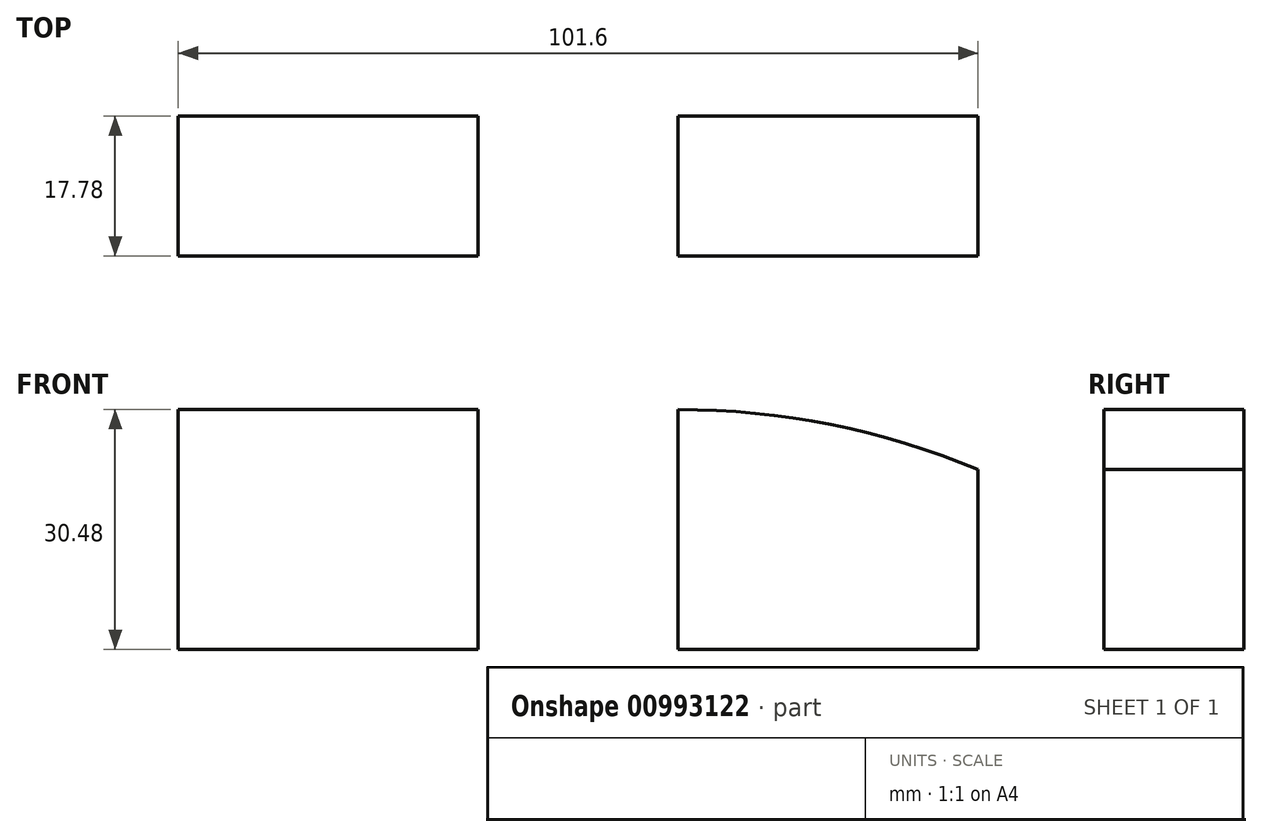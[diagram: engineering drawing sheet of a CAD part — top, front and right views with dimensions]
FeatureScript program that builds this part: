
annotation { "Feature Type Name" : "Feature", "Feature Type Description" : "" }
export const myFeature = defineFeature(function(context is Context, id is Id, definition is map)
    precondition{}
    {
        {
            var Q0;
            Q0=qCreatedBy(makeId("Top.planeOp"),FACE);
            var sketch = newSketch(context, id + "F0", { "sketchPlane" : qUnion([Q0])});
            skLineSegment(sketch, "E0.bottom", {"start": v(-38.1, -30.06) * mm, "end": v(63.5, -30.06) * mm});
            skLineSegment(sketch, "E0.top", {"start": v(-38.1, -47.84) * mm, "end": v(63.5, -47.84) * mm});
            skLineSegment(sketch, "E0.left", {"start": v(-38.1, -30.06) * mm, "end": v(-38.1, -47.84) * mm});
            skLineSegment(sketch, "E0.right", {"start": v(63.5, -30.06) * mm, "end": v(63.5, -47.84) * mm});
            skLineSegment(sketch, "E1.bottom", {"start": v(0, -30.06) * mm, "end": v(25.4, -30.06) * mm});
            skLineSegment(sketch, "E1.top", {"start": v(0, -47.84) * mm, "end": v(25.4, -47.84) * mm});
            skLineSegment(sketch, "E1.left", {"start": v(0, -30.06) * mm, "end": v(0, -47.84) * mm});
            skLineSegment(sketch, "E1.right", {"start": v(25.4, -30.06) * mm, "end": v(25.4, -47.84) * mm});
            skSolve(sketch);
        }
        {
            var Q0;
            {var subQ0=sQuery(id+"F0.wireOp",EDGE,"E0.left");Q0=makeQuery(id+"F0.imprint","IMPRINT",FACE,{"disambiguationData":[TD([[makeQuery(id+"F0.imprint","IMPRINT",EDGE,{"derivedFrom":subQ0}),1.0]])]});}
            var Q1;
            Q1=makeQuery(id+"F0.imprint","IMPRINT",FACE,{"disambiguationData":[TD([[makeQuery(id+"F0.imprint","IMPRINT",EDGE,{"derivedFrom":sQuery(id+"F0.wireOp",EDGE,"E1.bottom")}),-1.0]])]});
            var Q2;
            {var subQ0=sQuery(id+"F0.wireOp",EDGE,"E0.right");Q2=makeQuery(id+"F0.imprint","IMPRINT",FACE,{"disambiguationData":[TD([[makeQuery(id+"F0.imprint","IMPRINT",EDGE,{"derivedFrom":subQ0}),-1.0]])]});}
            extrude(context, id + "F1", {"entities" : qUnion([Q0, Q1, Q2]), "oppositeDirection" : true, "depth" : 15.24 * mm, "offsetDistance" : 25.4 * mm});
        }
        {
            var Q0;
            {var subQ0=sQuery(id+"F0.wireOp",EDGE,"E0.left");Q0=makeQuery(id+"F0.imprint","IMPRINT",FACE,{"disambiguationData":[TD([[makeQuery(id+"F0.imprint","IMPRINT",EDGE,{"derivedFrom":subQ0}),1.0]])]});}
            var Q1;
            {var subQ0=sQuery(id+"F0.wireOp",EDGE,"E0.right");Q1=makeQuery(id+"F0.imprint","IMPRINT",FACE,{"disambiguationData":[TD([[makeQuery(id+"F0.imprint","IMPRINT",EDGE,{"derivedFrom":subQ0}),-1.0]])]});}
            extrude(context, id + "F2", {"entities" : qUnion([Q0, Q1]), "operationType" : NewBodyOperationType.ADD, "depth" : 15.24 * mm, "offsetDistance" : 25.4 * mm});
        }
        {
            var Q0;
            {var subQ0=sQuery(id+"F0.wireOp",EDGE,"E0.top");var subQ1=sQuery(id+"F0.wireOp",EDGE,"E1.top");Q0=makeQuery(id+"F2.boolean.opBoolean","MERGE",FACE,{"derivedFrom":[makeQuery(id+"F1.opExtrude","SWEPT_FACE",FACE,{"disambiguationData":[OSD([subQ0,subQ1])]}),makeQuery(id+"F2.opExtrude","SWEPT_FACE",FACE,{"disambiguationData":[OSD([subQ0]),TDD([makeQuery(id+"F0.imprint","IMPRINT",EDGE,{"disambiguationData":[TD([[makeQuery(id+"F0.imprint","INTERSECT",VERTEX,{"derivedFrom":[subQ0,sQuery(id+"F0.wireOp",EDGE,"E0.left")]}),-1.0]])],"derivedFrom":subQ0})])]}),makeQuery(id+"F2.opExtrude","SWEPT_FACE",FACE,{"disambiguationData":[OSD([subQ0]),TDD([makeQuery(id+"F0.imprint","IMPRINT",EDGE,{"disambiguationData":[TD([[makeQuery(id+"F0.imprint","INTERSECT",VERTEX,{"derivedFrom":[subQ0,sQuery(id+"F0.wireOp",EDGE,"E0.right")]}),1.0]])],"derivedFrom":subQ0})])]})]});}
            var sketch = newSketch(context, id + "F3", { "sketchPlane" : qUnion([Q0])});
            skArc(sketch, "E2", {"start": v(0, 15.24) * mm, "mid": v(-19.43, 13.32) * mm, "end": v(-38.1, 7.62) * mm});
            skPoint(sketch, "E2.endSnap0", {"position": v(0, 7.62) * mm});
            skArc(sketch, "E3", {"start": v(63.5, 7.62) * mm, "mid": v(44.83, 13.32) * mm, "end": v(25.4, 15.24) * mm});
            skPoint(sketch, "E3.startSnap0", {"position": v(25.4, 7.62) * mm});
            skSolve(sketch);
        }
        {
            var Q0;
            {var subQ0=sQuery(id+"F3.wireOp",EDGE,"E2");Q0=makeQuery(id+"F3.imprint","IMPRINT",FACE,{"disambiguationData":[TD([[makeQuery(id+"F3.imprint","IMPRINT",EDGE,{"derivedFrom":subQ0}),-1.0]])]});}
            var Q1;
            {var subQ0=sQuery(id+"F3.wireOp",EDGE,"E3");Q1=makeQuery(id+"F3.imprint","IMPRINT",FACE,{"disambiguationData":[TD([[makeQuery(id+"F3.imprint","IMPRINT",EDGE,{"derivedFrom":subQ0}),-1.0]])]});}
            extrude(context, id + "F4", {"entities" : qUnion([Q0, Q1]), "operationType" : NewBodyOperationType.REMOVE, "oppositeDirection" : true, "depth" : 25.4 * mm, "offsetDistance" : 25.4 * mm});
        }
    });
